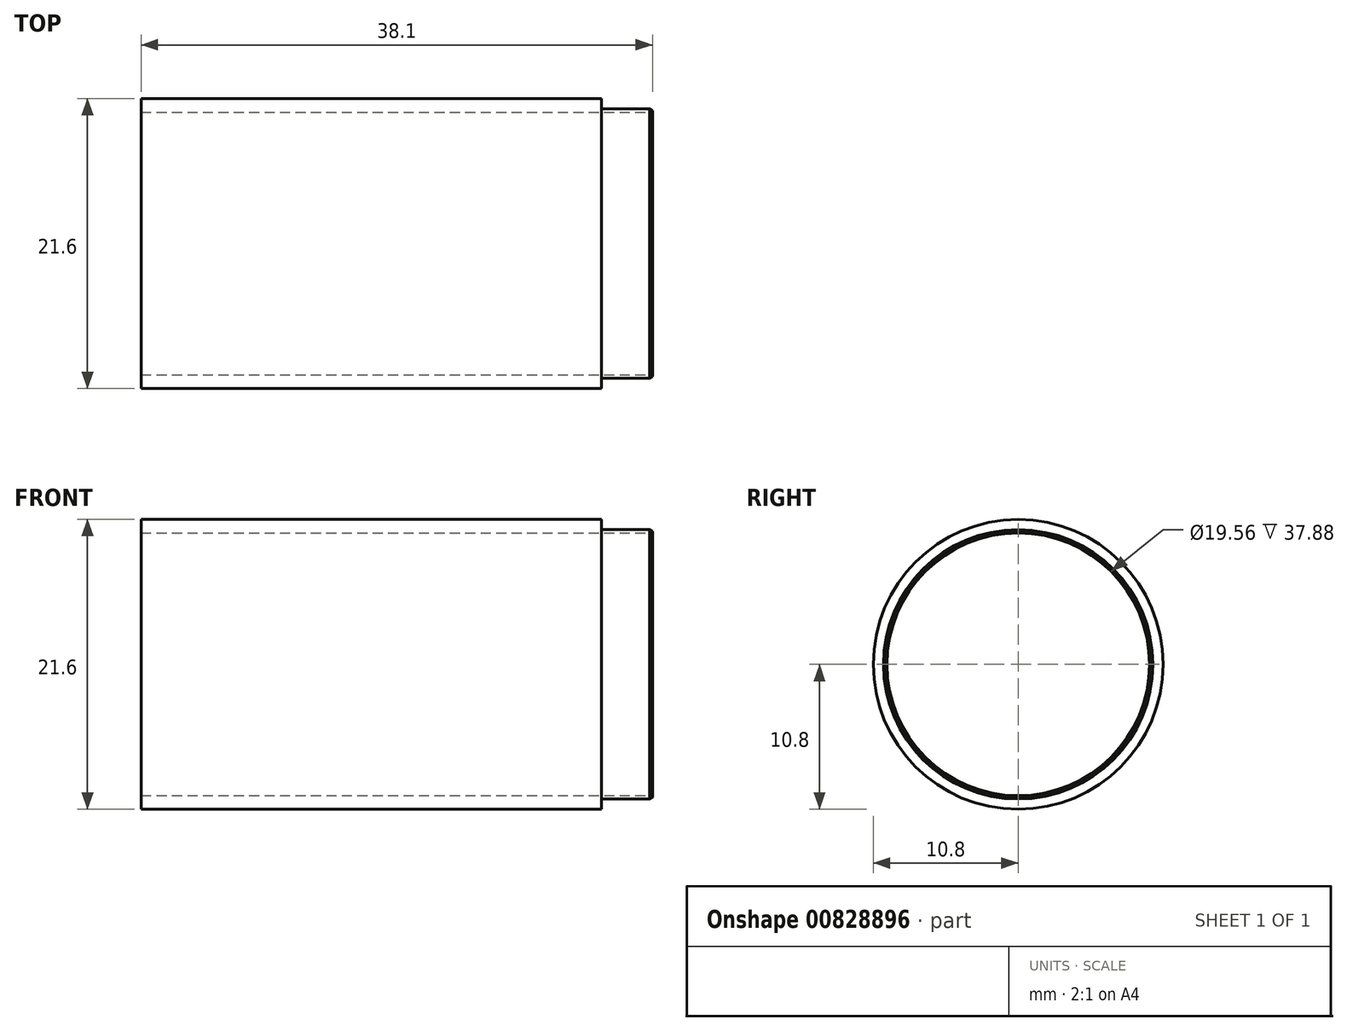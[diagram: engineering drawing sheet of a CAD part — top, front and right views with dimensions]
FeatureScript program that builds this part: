
annotation { "Feature Type Name" : "Feature", "Feature Type Description" : "" }
export const myFeature = defineFeature(function(context is Context, id is Id, definition is map)
    precondition{}
    {
        {
            var Q0;
            Q0=qCreatedBy(makeId("Front.planeOp"),FACE);
            var sketch = newSketch(context, id + "F0", { "sketchPlane" : qUnion([Q0])});
            skLineSegment(sketch, "E0", {"start": v(0, 9.78) * mm, "end": v(-38.1, 9.78) * mm});
            skLineSegment(sketch, "E1", {"start": v(0, 9.78) * mm, "end": v(0, 10.03) * mm});
            skLineSegment(sketch, "E2", {"start": v(0, 10.03) * mm, "end": v(-3.81, 10.03) * mm});
            skLineSegment(sketch, "E3", {"start": v(-3.81, 10.03) * mm, "end": v(-3.81, 10.8) * mm});
            skLineSegment(sketch, "E4", {"start": v(-3.81, 10.8) * mm, "end": v(-38.1, 10.8) * mm});
            skLineSegment(sketch, "E5", {"start": v(-38.1, 10.8) * mm, "end": v(-38.1, 9.78) * mm});
            skLineSegment(sketch, "E6", {"start": v(0, 0) * mm, "end": v(-38.1, 0) * mm, "construction": true});
            skSolve(sketch);
        }
        {
            var Q0;
            Q0=makeQuery(id+"F0.imprint","IMPRINT",FACE,{"disambiguationData":[TD([[makeQuery(id+"F0.imprint","IMPRINT",EDGE,{"derivedFrom":sQuery(id+"F0.wireOp",EDGE,"E0")}),-1.0]])]});
            var Q1;
            Q1=sQuery(id+"F0.wireOp",EDGE,"E6");
            revolve(context, id + "F1", {"surfaceOperationType" : NewSurfaceOperationType.NEW, "entities" : qUnion([Q0]), "axis" : qUnion([Q1]), "revolveType" : RevolveType.FULL});
        }
        {
            var Q0;
            Q0=makeQuery(id+"F1.opRevolve","SWEPT_EDGE",EDGE,{"disambiguationData":[OSD([sQuery(id+"F0.wireOp",EDGE,"E1"),sQuery(id+"F0.wireOp",EDGE,"E2")])]});
            var Q1;
            Q1=makeQuery(id+"F1.opRevolve","SWEPT_EDGE",EDGE,{"disambiguationData":[OSD([sQuery(id+"F0.wireOp",EDGE,"E0"),sQuery(id+"F0.wireOp",EDGE,"E1")])]});
            chamfer(context, id + "F2", {"entities" : qUnion([Q0, Q1]), "chamferType" : ChamferType.OFFSET_ANGLE, "width" : 0.13 * mm, "oppositeDirection" : false, "angle" : 60 * degree, "tangentPropagation" : true});
        }
    });
